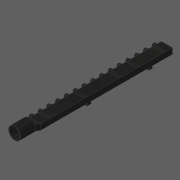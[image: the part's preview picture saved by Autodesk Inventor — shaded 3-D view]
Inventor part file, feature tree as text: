
AUTODESK INVENTOR PART (.ipt)
format: ipt  version: 2020 (Build 240168000, 168)  size: 574,976 bytes
history: native  units: in
note: dims shown in document units (in); Inventor stores cm internally (conversion verified against a paired STEP export)
features: other x11, extrude x6, loft x3, pattern_linear x1, projected_geometry x1
ambient origin geometry x8: Origin, YZ Plane, XZ Plane, XY Plane, X Axis, Y Axis, Z Axis, Center Point
bodies: Solid1 (feature_tree)
feature tree (22):
  other  "CrossSection1"
  other  "Box Sketch"
  extrude  "Box"  Depth=0.1181in
  other  "Fitting Plane"
  other  "Fitting"
  loft  "Fitting Entrance Loft"
  pattern_linear  "Channel Repetition"  Spacing1=0.0787in  [1 undecoded]
  extrude  "Small Tabs"  TaperAngle=0.0deg  [1 undecoded]
  extrude  "Big Tabs"  Depth=0.251in
  other  "Mouthpiece Plane"
  other  "Mouthpiece Sketch"
  loft  "Mouthpiece Loft (outer)"
  loft  "Mouthpiece Loft (inner)"
  extrude  "Mouthpiece"  Depth=0.0492in
  extrude  "Connector"  Depth=0.0315in
  extrude  "Shorten"  Depth=0.0938in
  other  "Fitting Sketch"
  other  "Fitting Entrance Loft From"
  projected_geometry  "Projected Loop1"
  other  "Small Tab Sketch"
  other  "Fitting Entrance Loft To"
  other  "Big Tab Sketch"
note: 2 required parameter values undecoded (feature->parameter linkage not recoverable at this tier; creation-order binding heuristic only, values carry confidence <= 0.55)
